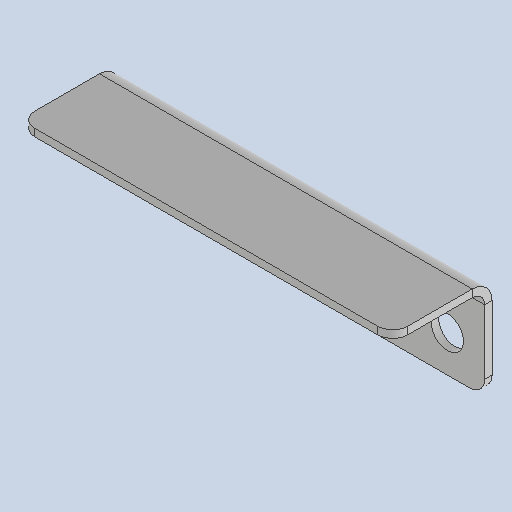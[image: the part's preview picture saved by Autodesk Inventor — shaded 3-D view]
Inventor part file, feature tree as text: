
AUTODESK INVENTOR PART (.ipt)
format: ipt  version: 2025 (Build 290162010, 162A)  size: 307,712 bytes
history: native  units: mm
features: sheet_metal_op x4, other x4, sketch x3, chamfer x1
ambient origin geometry x8: Origin, YZ Plane, XZ Plane, XY Plane, X Axis, Y Axis, Z Axis, Center Point
bodies: Body1 (feature_tree)
feature tree (12):
  sheet_metal_op  "Face2"
  sheet_metal_op  "Flange1"
  chamfer  "Corner Round6"
  sketch  "Sketch4"  dims[d36=150.0mm]
  other  "Plate2"
  sketch  "Sketch5"  dims[d37=40.0mm]
  sketch  "Sketch6"  dims[d38=3.0mm d39=120.0mm d40=15.0mm d41=13.0mm d42=3.0mm d43=0.0mm d44=3.0mm d45=1.5mm d46=6.0mm d47=5.0mm d48=40.0mm d49=90.0deg d50=5.0mm d51=12.0mm d52=3.0mm d53=5.0mm d54=6.0mm]
  other  "Plate3"
  sheet_metal_op  "Bend1"
  sheet_metal_op  "Corner1"
  other  "Cut1"
  other  "Definition1"
